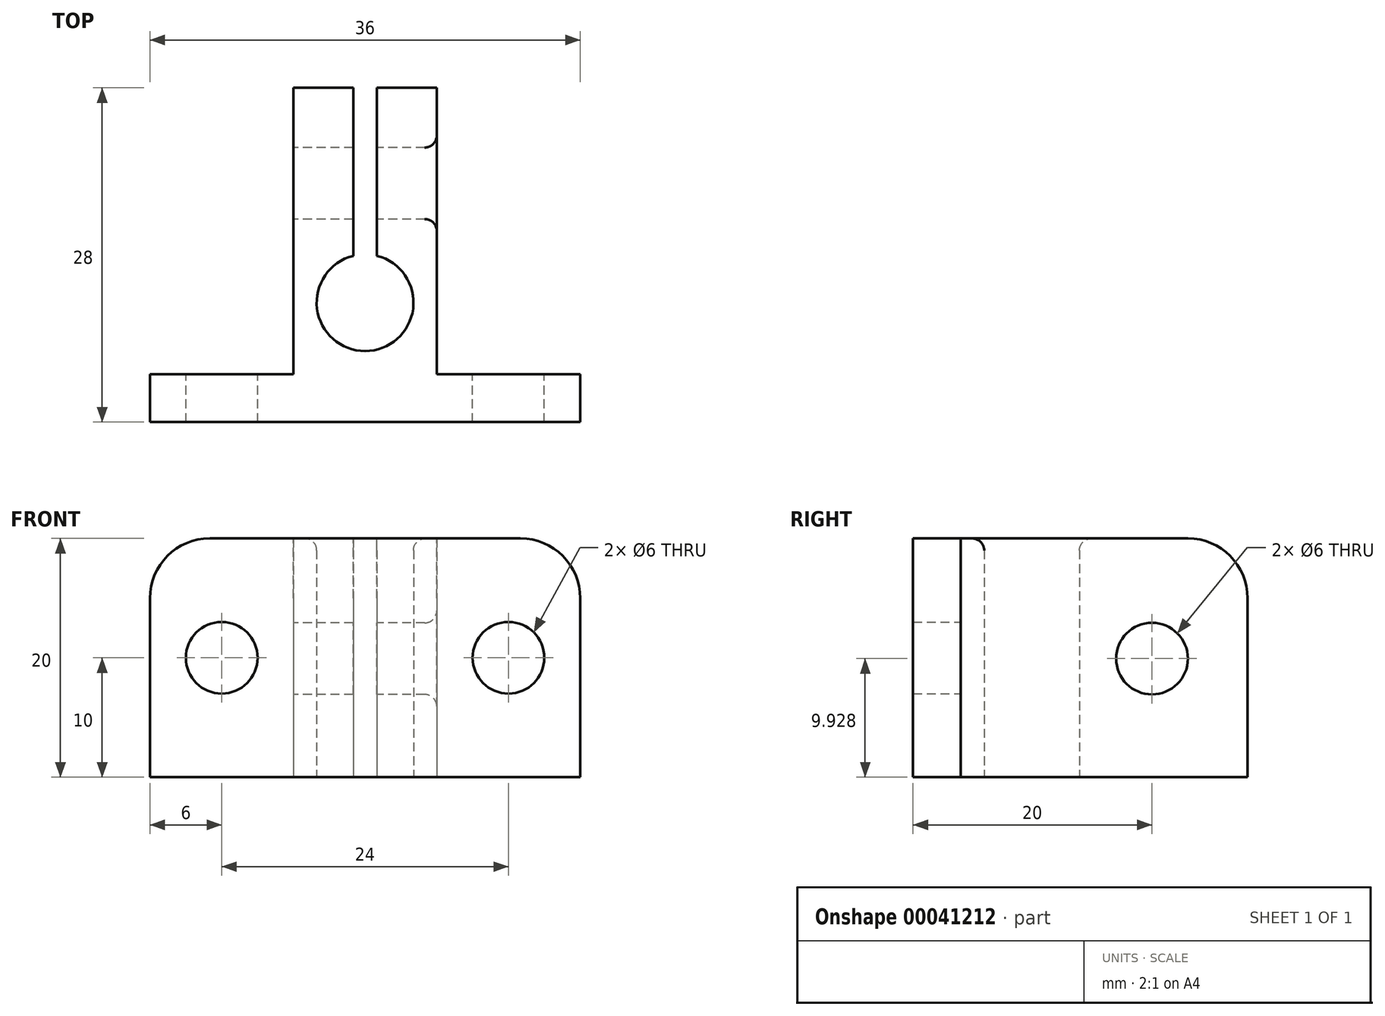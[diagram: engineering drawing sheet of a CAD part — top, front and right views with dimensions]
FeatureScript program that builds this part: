
annotation { "Feature Type Name" : "Feature", "Feature Type Description" : "" }
export const myFeature = defineFeature(function(context is Context, id is Id, definition is map)
    precondition{}
    {
        {
            var Q0;
            Q0=qCreatedBy(makeId("Top.planeOp"),FACE);
            var sketch = newSketch(context, id + "F0", { "sketchPlane" : qUnion([Q0])});
            skLineSegment(sketch, "E0", {"start": v(0, 28) * mm, "end": v(-6, 28) * mm});
            skLineSegment(sketch, "E1", {"start": v(-6, 28) * mm, "end": v(-6, 4) * mm});
            skLineSegment(sketch, "E2", {"start": v(-6, 4) * mm, "end": v(-18, 4) * mm});
            skLineSegment(sketch, "E3", {"start": v(-18, 4) * mm, "end": v(-18, 0) * mm});
            skLineSegment(sketch, "E4", {"start": v(-18, 0) * mm, "end": v(0, 0) * mm});
            skLineSegment(sketch, "E5.MirrorCS", {"start": v(18, 0) * mm, "end": v(0, 0) * mm});
            skLineSegment(sketch, "E6.MirrorCS", {"start": v(18, 4) * mm, "end": v(18, 0) * mm});
            skLineSegment(sketch, "E7.MirrorCS", {"start": v(6, 4) * mm, "end": v(18, 4) * mm});
            skLineSegment(sketch, "E8.MirrorCS", {"start": v(0, 28) * mm, "end": v(6, 28) * mm});
            skLineSegment(sketch, "E9.MirrorCS", {"start": v(6, 28) * mm, "end": v(6, 4) * mm});
            skCircle(sketch, "E10", {"center": v(0, 10) * mm, "radius": 4.05 * mm});
            skSolve(sketch);
        }
        {
            var Q0;
            Q0 = qSketchRegion(id + "F0", true);
            extrude(context, id + "F1", {"entities" : qUnion([Q0]), "depth" : 20 * mm});
        }
        {
            var Q0;
            Q0=makeQuery(id+"F1.opExtrude","CAP_FACE",FACE,{"disambiguationData":[OSD([sQuery(id+"F0.wireOp",EDGE,"E0"),sQuery(id+"F0.wireOp",EDGE,"E1"),sQuery(id+"F0.wireOp",EDGE,"E2"),sQuery(id+"F0.wireOp",EDGE,"E3"),sQuery(id+"F0.wireOp",EDGE,"E4"),sQuery(id+"F0.wireOp",EDGE,"E5.MirrorCS"),sQuery(id+"F0.wireOp",EDGE,"E6.MirrorCS"),sQuery(id+"F0.wireOp",EDGE,"E7.MirrorCS"),sQuery(id+"F0.wireOp",EDGE,"E8.MirrorCS"),sQuery(id+"F0.wireOp",EDGE,"E9.MirrorCS"),sQuery(id+"F0.wireOp",EDGE,"E10")])],"isStart":false});
            var sketch = newSketch(context, id + "F2", { "sketchPlane" : qUnion([Q0])});
            skLineSegment(sketch, "E11.rect.bottom", {"start": v(1, 8.56) * mm, "end": v(-1, 8.56) * mm});
            skLineSegment(sketch, "E11.rect.top", {"start": v(1, 34.1) * mm, "end": v(-1, 34.1) * mm});
            skLineSegment(sketch, "E11.rect.left", {"start": v(1, 8.56) * mm, "end": v(1, 34.1) * mm});
            skLineSegment(sketch, "E11.rect.right", {"start": v(-1, 8.56) * mm, "end": v(-1, 34.1) * mm});
            skPoint(sketch, "E11.rect.middle", {"position": v(0, 21.33) * mm});
            skSolve(sketch);
        }
        {
            var Q0;
            Q0 = qSketchRegion(id + "F2", true);
            extrude(context, id + "F3", {"entities" : qUnion([Q0]), "operationType" : NewBodyOperationType.REMOVE, "oppositeDirection" : true, "depth" : 25 * mm});
        }
        {
            var Q0;
            Q0=makeQuery(id+"F1.opExtrude","SWEPT_FACE",FACE,{"disambiguationData":[OSD([sQuery(id+"F0.wireOp",EDGE,"E1")])]});
            var sketch = newSketch(context, id + "F4", { "sketchPlane" : qUnion([Q0])});
            skCircle(sketch, "E12", {"center": v(-20, 9.93) * mm, "radius": 3 * mm});
            skSolve(sketch);
        }
        {
            var Q0;
            Q0 = qSketchRegion(id + "F4", true);
            extrude(context, id + "F5", {"entities" : qUnion([Q0]), "operationType" : NewBodyOperationType.REMOVE, "oppositeDirection" : true, "depth" : 25 * mm});
        }
        {
            var Q0;
            Q0=makeQuery(id+"F1.opExtrude","SWEPT_FACE",FACE,{"disambiguationData":[OSD([sQuery(id+"F0.wireOp",EDGE,"E2")])]});
            var sketch = newSketch(context, id + "F6", { "sketchPlane" : qUnion([Q0])});
            skCircle(sketch, "E13", {"center": v(12, 10) * mm, "radius": 3 * mm});
            skCircle(sketch, "E14.MirrorC", {"center": v(-12, 10) * mm, "radius": 3 * mm});
            skSolve(sketch);
        }
        {
            var Q0;
            Q0 = qSketchRegion(id + "F6", true);
            extrude(context, id + "F7", {"entities" : qUnion([Q0]), "operationType" : NewBodyOperationType.REMOVE, "oppositeDirection" : true, "depth" : 25 * mm});
        }
        {
            var Q0;
            {var subQ0=sQuery(id+"F0.wireOp",EDGE,"E0");var subQ1=sQuery(id+"F0.wireOp",EDGE,"E8.MirrorCS");var subQ2=sQuery(id+"F0.wireOp",EDGE,"E9.MirrorCS");Q0=makeQuery(id+"F3.boolean.opBoolean","SPLIT",EDGE,{"disambiguationData":[TD([makeQuery(id+"F1.opExtrude","SWEPT_FACE",FACE,{"disambiguationData":[OSD([subQ2])]})])],"derivedFrom":makeQuery(id+"F1.opExtrude","CAP_EDGE",EDGE,{"disambiguationData":[OSD([subQ0,subQ1])],"isStart":false})});}
            var Q1;
            {var subQ0=sQuery(id+"F0.wireOp",EDGE,"E0");var subQ1=sQuery(id+"F0.wireOp",EDGE,"E8.MirrorCS");var subQ2=sQuery(id+"F0.wireOp",EDGE,"E1");Q1=makeQuery(id+"F3.boolean.opBoolean","SPLIT",EDGE,{"disambiguationData":[TD([makeQuery(id+"F1.opExtrude","SWEPT_FACE",FACE,{"disambiguationData":[OSD([subQ2])]})])],"derivedFrom":makeQuery(id+"F1.opExtrude","CAP_EDGE",EDGE,{"disambiguationData":[OSD([subQ0,subQ1])],"isStart":false})});}
            var Q2;
            Q2=makeQuery(id+"F1.opExtrude","CAP_EDGE",EDGE,{"disambiguationData":[OSD([sQuery(id+"F0.wireOp",EDGE,"E3")])],"isStart":false});
            var Q3;
            Q3=makeQuery(id+"F1.opExtrude","CAP_EDGE",EDGE,{"disambiguationData":[OSD([sQuery(id+"F0.wireOp",EDGE,"E6.MirrorCS")])],"isStart":false});
            fillet(context, id + "F8", {"entities" : qUnion([Q0, Q1, Q2, Q3]), "radius" : 5 * mm, "tangentPropagation" : true, "allowEdgeOverflow" : false});
        }
        {
            var Q0;
            Q0=makeQuery(id+"F1.opExtrude","CAP_EDGE",EDGE,{"disambiguationData":[OSD([sQuery(id+"F0.wireOp",EDGE,"E10")])],"isStart":false});
            var Q1;
            Q1=makeQuery(id+"F7.boolean.opBoolean","COPY",EDGE,{"derivedFrom":makeQuery(id+"F7.opExtrude","CAP_EDGE",EDGE,{"disambiguationData":[OSD([sQuery(id+"F6.wireOp",EDGE,"E13")])],"isStart":true})});
            var Q2;
            Q2=makeQuery(id+"F7.boolean.opBoolean","COPY",EDGE,{"derivedFrom":makeQuery(id+"F7.opExtrude","CAP_EDGE",EDGE,{"disambiguationData":[OSD([sQuery(id+"F6.wireOp",EDGE,"E14.MirrorC")])],"isStart":true})});
            var Q3;
            Q3=makeQuery(id+"F5.boolean.opBoolean","COPY",EDGE,{"derivedFrom":makeQuery(id+"F5.opExtrude","CAP_EDGE",EDGE,{"disambiguationData":[OSD([sQuery(id+"F4.wireOp",EDGE,"E12")])],"isStart":true})});
            var Q4;
            Q4=makeQuery(id+"F5.boolean.opBoolean","INTERSECT",EDGE,{"derivedFrom":[makeQuery(id+"F1.opExtrude","SWEPT_FACE",FACE,{"disambiguationData":[OSD([sQuery(id+"F0.wireOp",EDGE,"E9.MirrorCS")])]}),makeQuery(id+"F5.opExtrude","SWEPT_FACE",FACE,{"disambiguationData":[OSD([sQuery(id+"F4.wireOp",EDGE,"E12")])]})]});
            fillet(context, id + "F9", {"entities" : qUnion([Q0, Q1, Q2, Q3, Q4]), "radius" : 1 * mm, "tangentPropagation" : true, "allowEdgeOverflow" : false});
        }
    });
